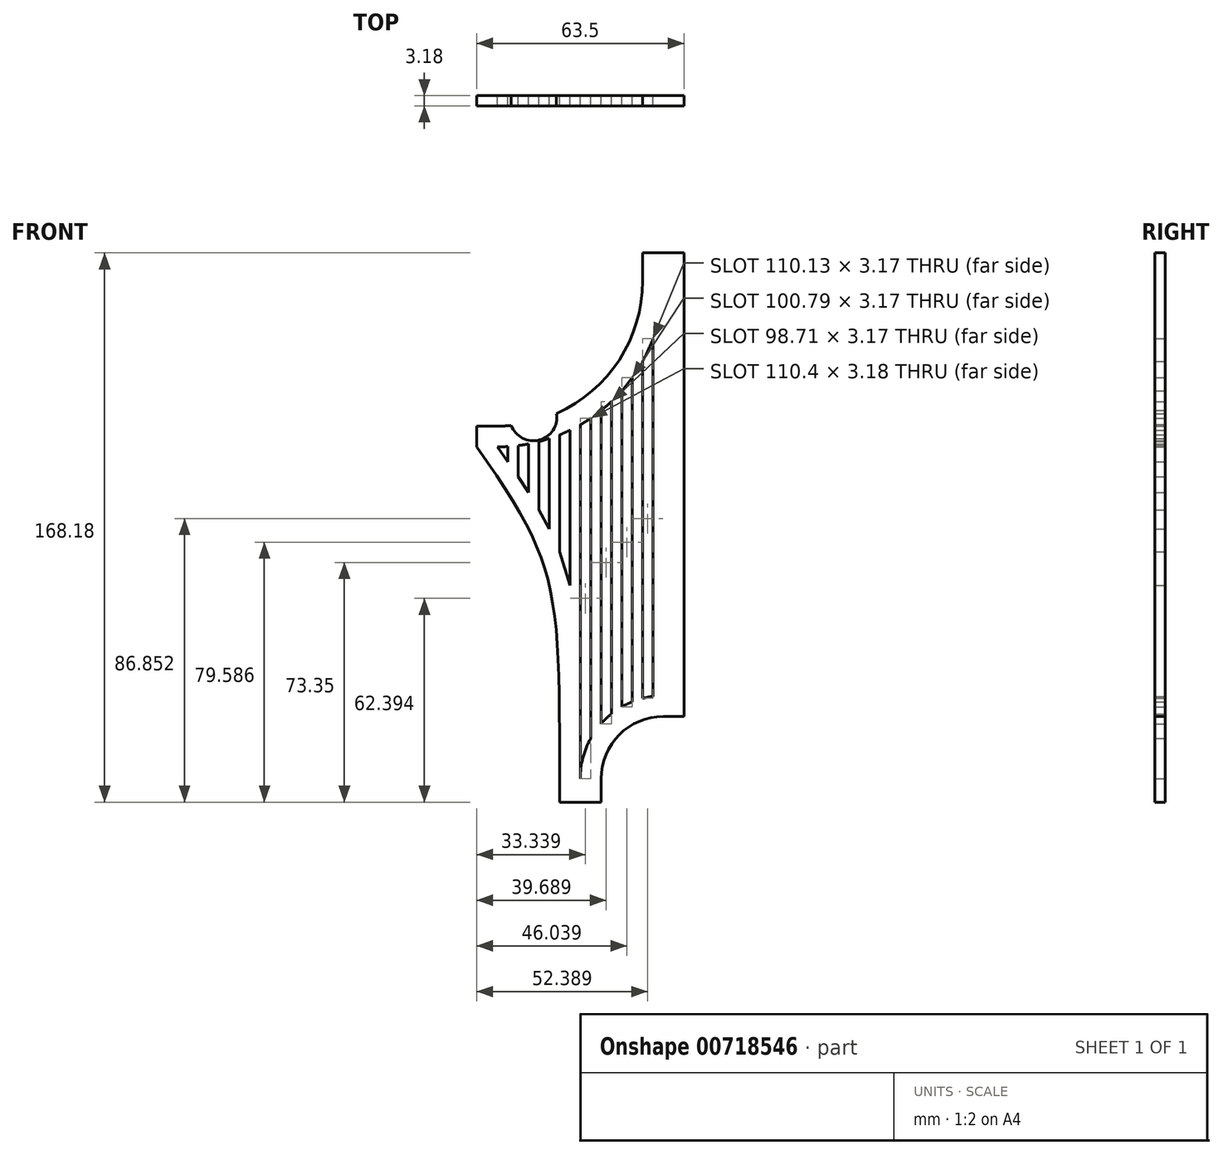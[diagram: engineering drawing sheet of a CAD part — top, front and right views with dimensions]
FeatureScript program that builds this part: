
annotation { "Feature Type Name" : "Feature", "Feature Type Description" : "" }
export const myFeature = defineFeature(function(context is Context, id is Id, definition is map)
    precondition{}
    {
        {
            var Q0;
            Q0=qCreatedBy(makeId("Front.planeOp"),FACE);
            var sketch = newSketch(context, id + "F0", { "sketchPlane" : qUnion([Q0])});
            skLineSegment(sketch, "E0", {"start": v(13.78, 20.14) * mm, "end": v(13.78, 70.94) * mm, "construction": true});
            skLineSegment(sketch, "E1", {"start": v(13.78, 20.14) * mm, "end": v(13.78, -56.06) * mm, "construction": true});
            skLineSegment(sketch, "E2", {"start": v(20.13, 79.53) * mm, "end": v(20.13, -62.4) * mm});
            skLineSegment(sketch, "E3", {"start": v(20.13, -62.4) * mm, "end": v(13.78, -62.4) * mm});
            skArc(sketch, "E4", {"start": v(13.78, -62.4) * mm, "mid": v(0.31, -67.99) * mm, "end": v(-5.27, -81.46) * mm});
            skLineSegment(sketch, "E5", {"start": v(-5.27, -81.46) * mm, "end": v(-5.27, -88.65) * mm});
            skLineSegment(sketch, "E6", {"start": v(-5.27, -88.65) * mm, "end": v(-11.62, -88.65) * mm});
            skLineSegment(sketch, "E7", {"start": v(-17.97, -88.65) * mm, "end": v(-11.62, -88.65) * mm});
            skArc(sketch, "E8", {"start": v(7.43, 70.94) * mm, "mid": v(-5.59, 39.51) * mm, "end": v(-37.02, 26.5) * mm});
            skLineSegment(sketch, "E9", {"start": v(20.13, 79.53) * mm, "end": v(7.43, 79.53) * mm});
            skLineSegment(sketch, "E10", {"start": v(7.43, 79.53) * mm, "end": v(7.43, 70.94) * mm});
            skLineSegment(sketch, "E11", {"start": v(-43.37, 20.15) * mm, "end": v(-43.37, 26.5) * mm});
            skLineSegment(sketch, "E12", {"start": v(-43.37, 26.5) * mm, "end": v(-37.02, 26.5) * mm});
            skFitSpline(sketch, "E13", {"points": [v(-43.37, 20.14) * mm, v(-17.97, -81.46) * mm], "startDerivative": vector(76.2, -107.14) * mm, "endDerivative": vector(0, -173.8) * mm});
            skLineSegment(sketch, "E14", {"start": v(-17.97, -88.65) * mm, "end": v(-17.97, -81.46) * mm});
            skPoint(sketch, "E15.endSnap0", {"position": v(0.31, -67.99) * mm});
            skPoint(sketch, "E16", {"position": v(-33.84, 20.14) * mm});
            skPoint(sketch, "E17", {"position": v(-30.67, 20.14) * mm});
            skPoint(sketch, "E18", {"position": v(-27.5, 20.14) * mm});
            skPoint(sketch, "E19", {"position": v(-24.32, 20.14) * mm});
            skPoint(sketch, "E20", {"position": v(-21.14, 20.14) * mm});
            skPoint(sketch, "E21", {"position": v(-17.97, 20.14) * mm});
            skPoint(sketch, "E22", {"position": v(-14.8, 20.14) * mm});
            skPoint(sketch, "E23", {"position": v(-11.62, 20.14) * mm});
            skPoint(sketch, "E24", {"position": v(-8.44, 20.14) * mm});
            skPoint(sketch, "E25", {"position": v(-5.27, 20.14) * mm});
            skPoint(sketch, "E26", {"position": v(4.26, 20.14) * mm});
            skPoint(sketch, "E27", {"position": v(7.43, 20.14) * mm});
            skPoint(sketch, "E28", {"position": v(10.6, 20.14) * mm});
            skPoint(sketch, "E29", {"position": v(-2.1, 20.14) * mm});
            skPoint(sketch, "E30", {"position": v(1.08, 20.14) * mm});
            skLineSegment(sketch, "E31", {"start": v(10.6, 20.14) * mm, "end": v(10.6, 53.27) * mm});
            skLineSegment(sketch, "E32", {"start": v(10.6, 20.14) * mm, "end": v(10.6, -56.25) * mm});
            skLineSegment(sketch, "E33", {"start": v(7.43, 20.14) * mm, "end": v(7.43, 46.35) * mm});
            skLineSegment(sketch, "E34", {"start": v(7.43, 20.14) * mm, "end": v(7.43, -56.86) * mm});
            skLineSegment(sketch, "E35", {"start": v(4.26, 20.14) * mm, "end": v(4.26, -57.9) * mm});
            skLineSegment(sketch, "E36", {"start": v(1.08, 20.14) * mm, "end": v(1.08, -59.46) * mm});
            skLineSegment(sketch, "E37", {"start": v(-2.1, 20.14) * mm, "end": v(-2.1, -61.63) * mm});
            skLineSegment(sketch, "E38", {"start": v(-5.27, 20.14) * mm, "end": v(-5.27, -64.66) * mm});
            skLineSegment(sketch, "E39", {"start": v(-8.44, 20.14) * mm, "end": v(-8.44, -69.16) * mm});
            skLineSegment(sketch, "E40", {"start": v(-11.62, 20.14) * mm, "end": v(-11.62, -81.46) * mm});
            skLineSegment(sketch, "E41", {"start": v(-14.8, 20.14) * mm, "end": v(-14.8, -22.32) * mm});
            skLineSegment(sketch, "E42", {"start": v(-17.97, 20.14) * mm, "end": v(-17.97, -12.04) * mm});
            skLineSegment(sketch, "E43", {"start": v(-21.14, 20.14) * mm, "end": v(-21.14, -4.94) * mm});
            skLineSegment(sketch, "E44", {"start": v(-24.32, 20.14) * mm, "end": v(-24.32, 0.9) * mm});
            skLineSegment(sketch, "E45", {"start": v(-27.5, 20.14) * mm, "end": v(-27.5, 6.12) * mm});
            skLineSegment(sketch, "E46", {"start": v(-30.67, 20.14) * mm, "end": v(-30.67, 10.98) * mm});
            skLineSegment(sketch, "E47", {"start": v(-33.84, 20.14) * mm, "end": v(-33.84, 15.63) * mm});
            skLineSegment(sketch, "E48", {"start": v(4.26, 20.14) * mm, "end": v(4.26, 41.33) * mm});
            skLineSegment(sketch, "E49", {"start": v(1.08, 20.14) * mm, "end": v(1.08, 37.34) * mm});
            skLineSegment(sketch, "E50", {"start": v(-2.1, 20.14) * mm, "end": v(-2.1, 34.05) * mm});
            skLineSegment(sketch, "E51", {"start": v(-5.27, 20.14) * mm, "end": v(-5.27, 31.29) * mm});
            skLineSegment(sketch, "E52", {"start": v(-8.44, 20.14) * mm, "end": v(-8.44, 28.94) * mm});
            skLineSegment(sketch, "E53", {"start": v(-11.62, 20.14) * mm, "end": v(-11.62, 26.95) * mm});
            skLineSegment(sketch, "E54", {"start": v(-14.8, 20.14) * mm, "end": v(-14.8, 25.26) * mm});
            skLineSegment(sketch, "E55", {"start": v(-17.97, 20.14) * mm, "end": v(-17.97, 23.85) * mm});
            skLineSegment(sketch, "E56", {"start": v(-21.14, 20.14) * mm, "end": v(-21.14, 22.69) * mm});
            skLineSegment(sketch, "E57", {"start": v(-24.32, 20.14) * mm, "end": v(-24.32, 21.76) * mm});
            skLineSegment(sketch, "E58", {"start": v(-27.5, 20.14) * mm, "end": v(-27.5, 21.05) * mm});
            skLineSegment(sketch, "E59", {"start": v(-30.67, 20.14) * mm, "end": v(-30.67, 20.54) * mm});
            skLineSegment(sketch, "E60", {"start": v(13.78, -56.06) * mm, "end": v(13.78, 70.94) * mm});
            skArc(sketch, "E61", {"start": v(-2.1, 34.05) * mm, "mid": v(-3.65, 32.64) * mm, "end": v(-5.27, 31.29) * mm});
            skFitSpline(sketch, "E62", {"points": [v(-33.84, 20.24) * mm, v(-33.84, 20.14) * mm], "startDerivative": vector(0, -0.1) * mm, "endDerivative": vector(0, -0.1) * mm});
            skPoint(sketch, "E63", {"position": v(-37.02, 20.14) * mm});
            skArc(sketch, "E64", {"start": v(1.08, 37.34) * mm, "mid": v(2.72, 39.3) * mm, "end": v(4.26, 41.33) * mm});
            skArc(sketch, "E65", {"start": v(7.43, 46.35) * mm, "mid": v(9.15, 49.75) * mm, "end": v(10.6, 53.27) * mm});
            skArc(sketch, "E66", {"start": v(-8.44, 28.94) * mm, "mid": v(-10.01, 27.92) * mm, "end": v(-11.62, 26.95) * mm});
            skArc(sketch, "E67", {"start": v(-14.8, 25.26) * mm, "mid": v(-16.37, 24.53) * mm, "end": v(-17.97, 23.85) * mm});
            skArc(sketch, "E68", {"start": v(-21.14, 22.69) * mm, "mid": v(-22.72, 22.2) * mm, "end": v(-24.32, 21.76) * mm});
            skArc(sketch, "E69", {"start": v(-27.5, 21.05) * mm, "mid": v(-29.08, 20.77) * mm, "end": v(-30.67, 20.54) * mm});
            skArc(sketch, "E70", {"start": v(-33.84, 20.24) * mm, "mid": v(-35.43, 20.17) * mm, "end": v(-37.02, 20.14) * mm});
            skArc(sketch, "E71", {"start": v(10.6, -56.25) * mm, "mid": v(9, -56.5) * mm, "end": v(7.43, -56.86) * mm});
            skArc(sketch, "E72", {"start": v(4.26, -57.9) * mm, "mid": v(2.64, -58.63) * mm, "end": v(1.08, -59.46) * mm});
            skArc(sketch, "E73", {"start": v(-2.1, -61.63) * mm, "mid": v(-3.75, -63.07) * mm, "end": v(-5.27, -64.66) * mm});
            skArc(sketch, "E74", {"start": v(-8.44, -69.16) * mm, "mid": v(-10.81, -75.1) * mm, "end": v(-11.62, -81.46) * mm});
            skFitSpline(sketch, "E75", {"points": [v(-37.02, 20.14) * mm, v(-33.84, 15.63) * mm], "startDerivative": vector(3.17, -4.51) * mm, "endDerivative": vector(3.17, -4.51) * mm});
            skLineSegment(sketch, "E76", {"start": v(-30.67, 10.98) * mm, "end": v(-27.5, 6.12) * mm});
            skLineSegment(sketch, "E77", {"start": v(-24.32, 0.9) * mm, "end": v(-21.14, -4.94) * mm});
            skLineSegment(sketch, "E78", {"start": v(-17.97, -12.04) * mm, "end": v(-14.8, -22.32) * mm});
            skSolve(sketch);
        }
        {
            var Q0;
            Q0=qCreatedBy(makeId("Front.planeOp"),FACE);
            var sketch = newSketch(context, id + "F1", { "sketchPlane" : qUnion([Q0])});
            skLineSegment(sketch, "E79", {"start": v(-5.27, -81.46) * mm, "end": v(-5.27, -88.65) * mm});
            skLineSegment(sketch, "E80", {"start": v(-5.27, -88.65) * mm, "end": v(-11.62, -88.65) * mm});
            skLineSegment(sketch, "E81", {"start": v(-17.97, -88.65) * mm, "end": v(-11.62, -88.65) * mm});
            skFitSpline(sketch, "E82", {"points": [v(-43.37, 20.14) * mm, v(-17.97, -81.46) * mm], "startDerivative": vector(76.2, -107.14) * mm, "endDerivative": vector(0, -173.8) * mm});
            skLineSegment(sketch, "E83", {"start": v(-17.97, -88.65) * mm, "end": v(-17.97, -81.46) * mm});
            skArc(sketch, "E84", {"start": v(13.78, -62.4) * mm, "mid": v(0.31, -67.99) * mm, "end": v(-5.27, -81.46) * mm});
            skArc(sketch, "E85", {"start": v(7.43, 70.94) * mm, "mid": v(-5.64, 39.46) * mm, "end": v(-37.16, 26.5) * mm});
            skLineSegment(sketch, "E86", {"start": v(13.78, -62.4) * mm, "end": v(20.13, -62.4) * mm});
            skLineSegment(sketch, "E87", {"start": v(20.13, -62.4) * mm, "end": v(20.13, 79.53) * mm});
            skLineSegment(sketch, "E88", {"start": v(20.13, 79.53) * mm, "end": v(7.43, 79.53) * mm});
            skLineSegment(sketch, "E89", {"start": v(7.43, 70.94) * mm, "end": v(7.43, 79.53) * mm});
            skLineSegment(sketch, "E90", {"start": v(-37.16, 26.5) * mm, "end": v(-43.37, 26.5) * mm});
            skLineSegment(sketch, "E91", {"start": v(-43.37, 26.5) * mm, "end": v(-43.37, 20.14) * mm});
            skSolve(sketch);
        }
        {
            var Q0;
            Q0 = qSketchRegion(id + "F1", true);
            extrude(context, id + "F2", {"entities" : qUnion([Q0]), "depth" : 3.17 * mm, "offsetDistance" : 25.4 * mm});
        }
        {
            var Q0;
            Q0 = qSketchRegion(id + "F0", true);
            extrude(context, id + "F3", {"entities" : qUnion([Q0]), "operationType" : NewBodyOperationType.REMOVE, "depth" : 3.17 * mm, "offsetDistance" : 25.4 * mm});
        }
        {
            var Q0;
            Q0=qCreatedBy(makeId("Front.planeOp"),FACE);
            var sketch = newSketch(context, id + "F4", { "sketchPlane" : qUnion([Q0])});
            skCircle(sketch, "E92", {"center": v(-26.03, 29.22) * mm, "radius": 7.2 * mm});
            skSolve(sketch);
        }
        {
            var Q0;
            Q0 = qSketchRegion(id + "F4", true);
            extrude(context, id + "F5", {"entities" : qUnion([Q0]), "operationType" : NewBodyOperationType.REMOVE, "depth" : 25.4 * mm, "offsetDistance" : 25.4 * mm});
        }
    });
